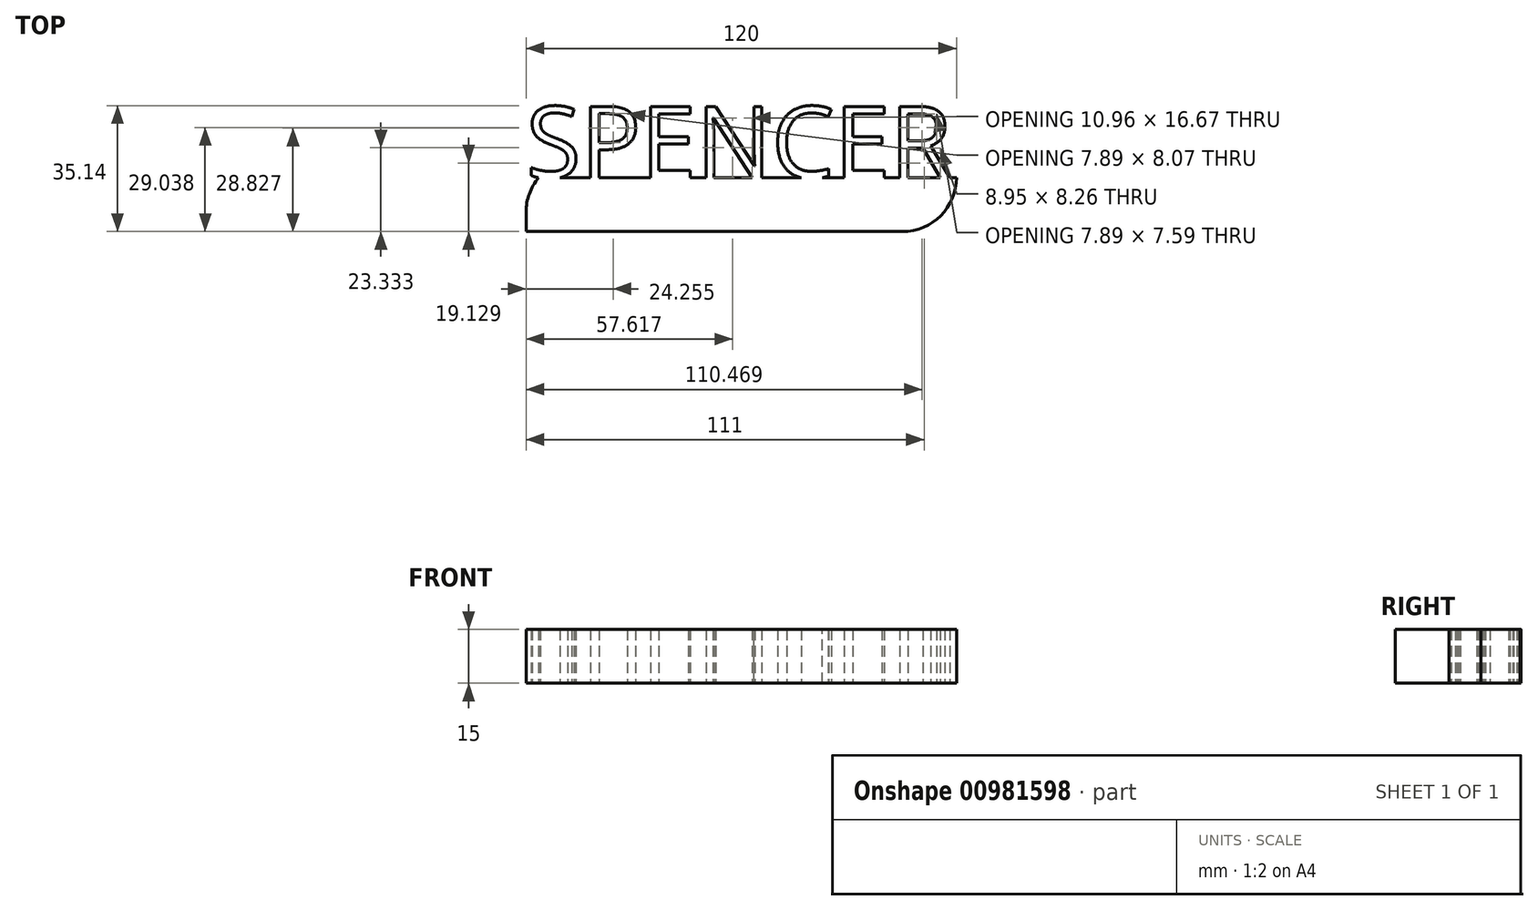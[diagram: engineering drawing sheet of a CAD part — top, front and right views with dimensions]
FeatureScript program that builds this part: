
annotation { "Feature Type Name" : "Feature", "Feature Type Description" : "" }
export const myFeature = defineFeature(function(context is Context, id is Id, definition is map)
    precondition{}
    {
        {
            var Q0;
            Q0=qCreatedBy(makeId("Top.planeOp"),FACE);
            var sketch = newSketch(context, id + "F0", { "sketchPlane" : qUnion([Q0])});
            skLineSegment(sketch, "E0.bottom", {"start": v(0, 0) * mm, "end": v(-120, 0) * mm});
            skLineSegment(sketch, "E0.top", {"start": v(0, 15) * mm, "end": v(-120, 15) * mm});
            skLineSegment(sketch, "E0.left", {"start": v(0, 0) * mm, "end": v(0, 15) * mm});
            skLineSegment(sketch, "E0.right", {"start": v(-120, 0) * mm, "end": v(-120, 15) * mm});
            skText(sketch, "E1", { "text": "SPENCER", "fontName": "OpenSans-Regular.ttf"});
            const initialGuessF0  = {"E1": [-0.12, 0.015, 1, 0, 0.02003]};
            skSetInitialGuess(sketch, initialGuessF0);
            skSolve(sketch);
        }
        {
            var Q0;
            Q0=qSketchRegion(id+"F0",true);
            extrude(context, id + "F1", {"entities" : qUnion([Q0]), "depth" : 15 * mm, "offsetDistance" : 25 * mm});
        }
        {
            var Q0;
            Q0=makeQuery(id+"F1.opExtrude","SWEPT_EDGE",EDGE,{"disambiguationData":[OSD([sQuery(id+"F0.wireOp",EDGE,"E0.top"),sQuery(id+"F0.wireOp",EDGE,"E0.right")])]});
            var Q1;
            Q1=makeQuery(id+"F1.opExtrude","SWEPT_EDGE",EDGE,{"disambiguationData":[OSD([sQuery(id+"F0.wireOp",EDGE,"E0.bottom"),sQuery(id+"F0.wireOp",EDGE,"E0.left")])]});
            fillet(context, id + "F2", {"entities" : qUnion([Q0, Q1]), "radius" : 15 * mm, "tangentPropagation" : true, "allowEdgeOverflow" : false});
        }
    });
